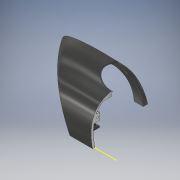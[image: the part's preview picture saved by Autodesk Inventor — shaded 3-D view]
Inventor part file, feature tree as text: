
AUTODESK INVENTOR PART (.ipt)
format: ipt  version: 2019 (Build 230136000, 136)  size: 1,320,960 bytes
history: native  units: mm
features: plane x27, sketch x24, extrude x11, fillet x6, mirror x5, loft x4, chamfer x3, other x1
ambient origin geometry x8: Origin, YZ Plane, XZ Plane, XY Plane, X Axis, Y Axis, Z Axis, Center Point
bodies: Body1 (feature_tree)
feature tree (81):
  sketch  "Sketch1"  dims[d2=55.0mm d5=-107.0mm d13=5.0mm d14=50.0mm]
  plane  "Work Plane1"
  sketch  "Sketch2"  dims[d15=70.0mm d16=5.0mm]
  sketch  "Sketch3"  dims[d17=0.0mm d18=90.0deg d19=0.0mm d20=90.0deg d21=0.0mm d22=90.0deg d23=2.0mm]
  plane  "Work Plane2"
  loft  "Loft2"
  mirror  "Mirror2"
  fillet  "Fillet1"  Radius=5.0mm
  fillet  "Fillet4"  Radius=50.0mm
  plane  "Work Plane3"
  plane  "Work Plane4"
  extrude  "Extrusion1"  Depth=5.0mm
  plane  "Work Plane5"
  extrude  "Extrusion2"  TaperAngle=0.0deg  [1 undecoded]
  fillet  "Fillet5"  [1 undecoded]
  mirror  "Mirror3"
  plane  "Work Plane22"
  plane  "Work Plane6"
  plane  "Work Plane7"
  fillet  "Fillet11"  Radius=2.0mm
  extrude  "Extrusion7"  Depth=87.5mm
  mirror  "Mirror4"
  plane  "Work Plane8"
  plane  "Work Plane9"
  sketch  "Sketch20"  dims[d42=2.0mm]
  plane  "Work Plane10"
  sketch  "Sketch21"  dims[d43=2.0mm]
  plane  "Work Plane11"
  sketch  "Sketch22"  dims[d44=2.0mm]
  loft  "Loft5"
  plane  "Work Plane13"
  sketch  "Sketch25"  dims[d45=2.0mm]
  plane  "Work Plane18"
  loft  "Loft6"
  mirror  "Mirror5"
  plane  "Work Plane19"
  extrude  "Extrusion9"  Depth=2.0mm
  fillet  "Fillet12"  Radius=2.0mm
  fillet  "Fillet14"  Radius=2.0mm
  plane  "Work Plane20"
  plane  "Work Plane21"
  plane  "Work Plane23"
  plane  "Work Plane24"
  plane  "Work Plane25"
  sketch  "Sketch33"  dims[d48=2.0mm]
  plane  "Work Plane26"
  sketch  "Sketch34"  dims[d49=2.0mm d50=2.0mm d51=1.0mm]
  plane  "Work Plane27"
  sketch  "Sketch35"  dims[d79=-25.0mm]
  plane  "Work Plane30"
  sketch  "Sketch38"  dims[d84=2.0mm]
  plane  "Work Plane31"
  plane  "Work Plane35"
  chamfer  "Chamfer7"  Distance=2.0mm
  chamfer  "Chamfer8"  Distance=28.0mm
  chamfer  "Chamfer9"  Distance=22.0mm
  loft  "Loft10"
  mirror  "Mirror9"
  plane  "Work Plane37"
  extrude  "Extrusion24"  Depth=70.0mm
  extrude  "Extrusion25"  Depth=3.0mm
  extrude  "Extrusion26"  Depth=20.0mm
  extrude  "Extrusion27"  TaperAngle=0.0deg  [1 undecoded]
  plane  "Work Plane38"
  extrude  "Extrusion28"  TaperAngle=0.0deg  [1 undecoded]
  extrude  "Extrusion29"  TaperAngle=0.0deg  [1 undecoded]
  extrude  "Extrusion30"  [1 undecoded]
  sketch  "Sketch4"  dims[d29=1.0mm d30=-4.5mm d31=87.5mm]
  sketch  "Sketch5"  dims[d32=0.0mm d33=0.0mm d34=-28.0mm]
  sketch  "Sketch6"  dims[d35=15.0mm d36=3.0mm]
  sketch  "Sketch17"  dims[d37=0.0mm d38=0.0mm d39=2.0mm d40=2.0mm d41=2.0mm]
  sketch  "Sketch27"  dims[d46=2.0mm]
  other  "Edges1"
  sketch  "Sketch28"  dims[d47=2.0mm]
  sketch  "Sketch47"  dims[d85=13.5mm]
  sketch  "Sketch48"  dims[d86=3.0mm]
  sketch  "Sketch49"  dims[d87=5.0mm]
  sketch  "Sketch50"  dims[d88=6.0mm d89=28.0mm d90=0.0mm d91=22.0mm d101=200.0mm]
  sketch  "Sketch51"  dims[d104=5.0mm d105=50.0mm d106=-80.0mm d107=45.0mm]
  sketch  "Sketch52"  dims[d108=3.0mm d109=70.0mm]
  sketch  "Sketch53"  dims[d110=80.0mm d111=3.0mm d112=20.0mm d123=0.0mm d124=90.0deg d125=0.0mm d126=90.0deg d127=0.0mm d128=90.0deg d129=-20.0mm d131=2.0mm d132=80.0mm d133=10.0mm d134=0.0mm d135=0.0mm d136=90.0deg d137=0.0mm d138=90.0deg d139=0.0mm d140=90.0deg d141=3.0mm d142=7.0mm d143=10.0mm d144=0.0mm d145=70.0mm d147=10.0mm d171=35.75mm d174=-8.25mm d177=20.0mm d179=30.0mm d180=5.0mm d181=41.5mm d182=15.0mm d183=10.0mm d184=5.0mm d200=-2.0mm d219=15.0mm d241=2.0mm d242=2.0mm d243=45.0deg d244=1.0mm d245=2.0mm d246=45.0deg d247=0.5mm d248=2.0mm d249=45.0deg d250=5.0mm d251=0.0mm d252=90.0deg d253=0.0mm d254=90.0deg d255=0.0mm d256=90.0deg d261=0.0mm d262=0.0mm d263=10.0mm d264=0.0mm d265=5.0mm d266=0.0mm d267=4.0mm d268=20.0mm d269=0.0mm d270=16.0mm d271=14.0mm d272=20.0mm d273=0.0mm d274=4.0mm d275=20.0mm d276=0.0mm d277=0.0mm d278=0.0mm]
note: 6 required parameter values undecoded (feature->parameter linkage not recoverable at this tier; creation-order binding heuristic only, values carry confidence <= 0.55)
